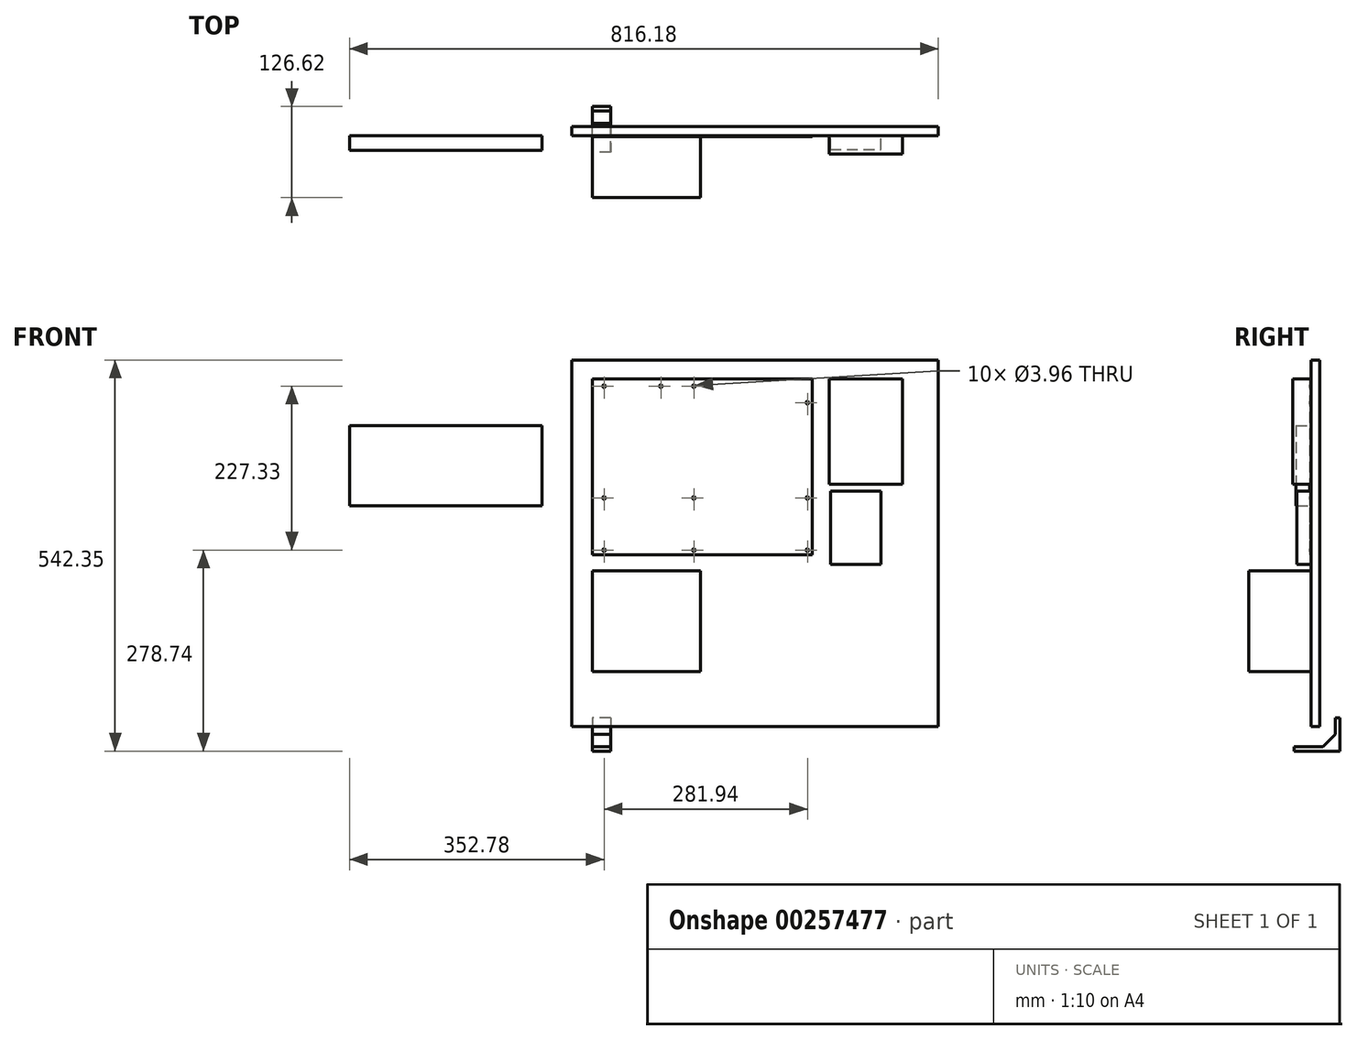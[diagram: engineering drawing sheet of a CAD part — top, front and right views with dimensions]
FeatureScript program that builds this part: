
annotation { "Feature Type Name" : "Feature", "Feature Type Description" : "" }
export const myFeature = defineFeature(function(context is Context, id is Id, definition is map)
    precondition{}
    {
        {
            var Q0;
            Q0=qCreatedBy(makeId("Front.planeOp"),FACE);
            var sketch = newSketch(context, id + "F0", { "sketchPlane" : qUnion([Q0])});
            skCircle(sketch, "E0", {"center": v(16.51, -10.16) * mm, "radius": 1.98 * mm});
            skCircle(sketch, "E1", {"center": v(140.97, -10.16) * mm, "radius": 1.98 * mm});
            skCircle(sketch, "E2", {"center": v(95.25, -10.16) * mm, "radius": 1.98 * mm});
            skCircle(sketch, "E3", {"center": v(298.45, -33.02) * mm, "radius": 1.98 * mm});
            skCircle(sketch, "E4", {"center": v(298.45, -165.1) * mm, "radius": 1.98 * mm});
            skCircle(sketch, "E5", {"center": v(298.45, -237.49) * mm, "radius": 1.98 * mm});
            skCircle(sketch, "E6", {"center": v(140.97, -165.1) * mm, "radius": 1.98 * mm});
            skCircle(sketch, "E7", {"center": v(140.97, -237.5) * mm, "radius": 1.98 * mm});
            skCircle(sketch, "E8", {"center": v(16.51, -165.1) * mm, "radius": 1.98 * mm});
            skCircle(sketch, "E9", {"center": v(16.51, -237.5) * mm, "radius": 1.98 * mm});
            skLineSegment(sketch, "E10.bottom", {"start": v(0, 0) * mm, "end": v(304.8, 0) * mm});
            skLineSegment(sketch, "E10.top", {"start": v(0, -243.84) * mm, "end": v(304.8, -243.84) * mm});
            skLineSegment(sketch, "E10.left", {"start": v(0, 0) * mm, "end": v(0, -243.84) * mm});
            skLineSegment(sketch, "E10.right", {"start": v(304.8, 0) * mm, "end": v(304.8, -243.84) * mm});
            skSolve(sketch);
        }
        {
            var Q0;
            Q0 = qSketchRegion(id + "F0", true);
            extrude(context, id + "F1", {"entities" : qUnion([Q0]), "depth" : 1.57 * mm});
        }
        {
            var Q0;
            Q0=qCreatedBy(makeId("Front.planeOp"),FACE);
            var sketch = newSketch(context, id + "F2", { "sketchPlane" : qUnion([Q0])});
            skLineSegment(sketch, "E11.bottom", {"start": v(150, -406.22) * mm, "end": v(0, -406.22) * mm});
            skLineSegment(sketch, "E11.top", {"start": v(150, -266.22) * mm, "end": v(0, -266.22) * mm});
            skLineSegment(sketch, "E11.left", {"start": v(150, -406.22) * mm, "end": v(150, -266.22) * mm});
            skLineSegment(sketch, "E11.right", {"start": v(0, -406.22) * mm, "end": v(0, -266.22) * mm});
            skSolve(sketch);
        }
        {
            var Q0;
            Q0 = qSketchRegion(id + "F2", true);
            extrude(context, id + "F3", {"entities" : qUnion([Q0]), "depth" : 86 * mm});
        }
        {
            var Q0;
            Q0=qCreatedBy(makeId("Front.planeOp"),FACE);
            var sketch = newSketch(context, id + "F4", { "sketchPlane" : qUnion([Q0])});
            skLineSegment(sketch, "E12.bottom", {"start": v(-69.57, -65.05) * mm, "end": v(-336.27, -65.05) * mm});
            skLineSegment(sketch, "E12.top", {"start": v(-69.57, -176.2) * mm, "end": v(-336.27, -176.2) * mm});
            skLineSegment(sketch, "E12.left", {"start": v(-69.57, -65.05) * mm, "end": v(-69.57, -176.2) * mm});
            skLineSegment(sketch, "E12.right", {"start": v(-336.27, -65.05) * mm, "end": v(-336.27, -176.2) * mm});
            skSolve(sketch);
        }
        {
            var Q0;
            Q0 = qSketchRegion(id + "F4", true);
            extrude(context, id + "F5", {"entities" : qUnion([Q0]), "operationType" : NewBodyOperationType.ADD, "depth" : 20.32 * mm});
        }
        {
            var Q0;
            Q0=qCreatedBy(makeId("Front.planeOp"),FACE);
            var sketch = newSketch(context, id + "F6", { "sketchPlane" : qUnion([Q0])});
            skLineSegment(sketch, "E13.bottom", {"start": v(328.46, -146.05) * mm, "end": v(430.06, -146.05) * mm});
            skLineSegment(sketch, "E13.top", {"start": v(328.46, 0) * mm, "end": v(430.06, 0) * mm});
            skLineSegment(sketch, "E13.left", {"start": v(328.46, -146.05) * mm, "end": v(328.46, 0) * mm});
            skLineSegment(sketch, "E13.right", {"start": v(430.06, -146.05) * mm, "end": v(430.06, 0) * mm});
            skSolve(sketch);
        }
        {
            var Q0;
            Q0 = qSketchRegion(id + "F6", true);
            extrude(context, id + "F7", {"entities" : qUnion([Q0]), "depth" : 25.4 * mm});
        }
        {
            var Q0;
            Q0=qCreatedBy(makeId("Front.planeOp"),FACE);
            var sketch = newSketch(context, id + "F8", { "sketchPlane" : qUnion([Q0])});
            skLineSegment(sketch, "E14.bottom", {"start": v(330.23, -257.37) * mm, "end": v(400.08, -257.37) * mm});
            skLineSegment(sketch, "E14.top", {"start": v(330.23, -155.77) * mm, "end": v(400.08, -155.77) * mm});
            skLineSegment(sketch, "E14.left", {"start": v(330.23, -257.37) * mm, "end": v(330.23, -155.77) * mm});
            skLineSegment(sketch, "E14.right", {"start": v(400.08, -257.37) * mm, "end": v(400.08, -155.77) * mm});
            skSolve(sketch);
        }
        {
            var Q0;
            Q0 = qSketchRegion(id + "F8", true);
            extrude(context, id + "F9", {"entities" : qUnion([Q0]), "depth" : 19.05 * mm});
        }
        {
            var Q0;
            Q0=qCreatedBy(makeId("Front.planeOp"),FACE);
            var sketch = newSketch(context, id + "F10", { "sketchPlane" : qUnion([Q0])});
            skLineSegment(sketch, "E15.bottom", {"start": v(-28.09, 26.12) * mm, "end": v(479.91, 26.12) * mm});
            skLineSegment(sketch, "E15.top", {"start": v(-28.09, -481.88) * mm, "end": v(479.91, -481.88) * mm});
            skLineSegment(sketch, "E15.left", {"start": v(-28.09, 26.12) * mm, "end": v(-28.09, -481.88) * mm});
            skLineSegment(sketch, "E15.right", {"start": v(479.91, 26.12) * mm, "end": v(479.91, -481.88) * mm});
            skSolve(sketch);
        }
        {
            var Q0;
            Q0=makeQuery(id+"F10.imprint","IMPRINT",FACE,{"disambiguationData":[TD([[makeQuery(id+"F10.imprint","IMPRINT",EDGE,{"derivedFrom":sQuery(id+"F10.wireOp",EDGE,"E15.bottom")}),-1.0]])]});
            extrude(context, id + "F11", {"entities" : qUnion([Q0]), "oppositeDirection" : true, "depth" : 12.7 * mm});
        }
        {
            var Q0;
            Q0=qCreatedBy(makeId("Right.planeOp"),FACE);
            var sketch = newSketch(context, id + "F12", { "sketchPlane" : qUnion([Q0])});
            skLineSegment(sketch, "E16.bottom", {"start": v(34.27, -470.07) * mm, "end": v(40.62, -470.07) * mm});
            skLineSegment(sketch, "E16.left", {"start": v(34.27, -470.07) * mm, "end": v(34.27, -492.65) * mm});
            skLineSegment(sketch, "E16.right", {"start": v(40.62, -470.07) * mm, "end": v(40.62, -516.23) * mm});
            skLineSegment(sketch, "E17.top", {"start": v(17.04, -509.88) * mm, "end": v(-22.88, -509.88) * mm});
            skLineSegment(sketch, "E17.right", {"start": v(-22.88, -516.23) * mm, "end": v(-22.88, -509.88) * mm});
            skLineSegment(sketch, "E18", {"start": v(-22.88, -516.23) * mm, "end": v(40.62, -516.23) * mm});
            skLineSegment(sketch, "E19", {"start": v(17.04, -509.88) * mm, "end": v(34.27, -492.65) * mm});
            skSolve(sketch);
        }
        {
            var Q0;
            Q0 = qSketchRegion(id + "F12", true);
            extrude(context, id + "F13", {"entities" : qUnion([Q0]), "depth" : 25.4 * mm});
        }
    });
